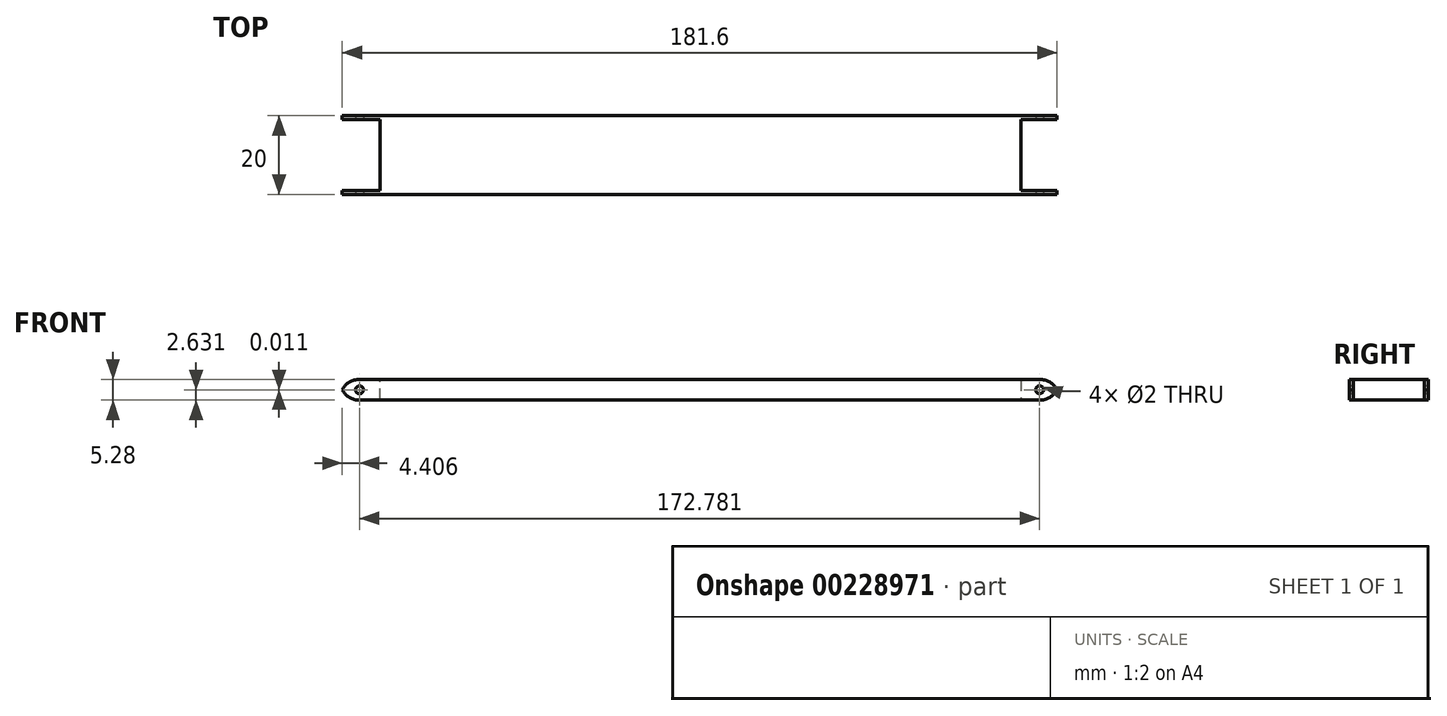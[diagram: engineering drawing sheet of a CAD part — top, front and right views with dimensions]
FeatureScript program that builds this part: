
annotation { "Feature Type Name" : "Feature", "Feature Type Description" : "" }
export const myFeature = defineFeature(function(context is Context, id is Id, definition is map)
    precondition{}
    {
        {
            var Q0;
            Q0=qCreatedBy(makeId("Front.planeOp"),FACE);
            var sketch = newSketch(context, id + "F0", { "sketchPlane" : qUnion([Q0])});
            skLineSegment(sketch, "E0.bottom", {"start": v(-74.93, 0) * mm, "end": v(107.85, 0) * mm});
            skLineSegment(sketch, "E0.top", {"start": v(-74.93, 5.28) * mm, "end": v(107.85, 5.28) * mm});
            skLineSegment(sketch, "E0.left", {"start": v(-74.93, 0) * mm, "end": v(-74.93, 5.28) * mm});
            skLineSegment(sketch, "E0.right", {"start": v(107.85, 0) * mm, "end": v(107.85, 5.28) * mm});
            skPoint(sketch, "E1", {"position": v(-74.93, 5.28) * mm});
            skPoint(sketch, "E2", {"position": v(-74.93, 0) * mm});
            skPoint(sketch, "E3", {"position": v(-69.93, 5.28) * mm});
            skPoint(sketch, "E4", {"position": v(-69.93, 0) * mm});
            skPoint(sketch, "E5", {"position": v(-74.36, 2.63) * mm});
            skPoint(sketch, "E6", {"position": v(-69.93, 2.63) * mm});
            skPoint(sketch, "E7", {"position": v(102.85, 5.28) * mm});
            skPoint(sketch, "E8", {"position": v(102.85, 0) * mm});
            skPoint(sketch, "E9", {"position": v(107.26, 2.64) * mm});
            skPoint(sketch, "E10", {"position": v(102.85, 2.64) * mm});
            skSolve(sketch);
        }
        {
            var Q0;
            Q0=makeQuery(id+"F0.imprint","IMPRINT",FACE,{"disambiguationData":[TD([[makeQuery(id+"F0.imprint","IMPRINT",EDGE,{"derivedFrom":sQuery(id+"F0.wireOp",EDGE,"E0.bottom")}),1.0]])]});
            extrude(context, id + "F1", {"entities" : qUnion([Q0]), "oppositeDirection" : true, "depth" : 20 * mm});
        }
        {
            var Q0;
            Q0=makeQuery(id+"F1.opExtrude","SWEPT_EDGE",EDGE,{"disambiguationData":[OSD([sQuery(id+"F0.wireOp",EDGE,"E0.top"),sQuery(id+"F0.wireOp",EDGE,"E0.left")])]});
            var Q1;
            Q1=makeQuery(id+"F1.opExtrude","SWEPT_EDGE",EDGE,{"disambiguationData":[OSD([sQuery(id+"F0.wireOp",EDGE,"E0.bottom"),sQuery(id+"F0.wireOp",EDGE,"E0.left")])]});
            fillet(context, id + "F2", {"entities" : qUnion([Q0, Q1]), "radius" : 5 * mm, "tangentPropagation" : true, "allowEdgeOverflow" : false});
        }
        {
            var Q0;
            Q0=sQuery(id+"F0.wireOp",VERTEX,"E6");
            var Q1;
            Q1=makeQuery(id+"F1.opExtrude","SWEPT_BODY",BODY,{"disambiguationData":[OSD([sQuery(id+"F0.wireOp",EDGE,"E0.bottom"),sQuery(id+"F0.wireOp",EDGE,"E0.top"),sQuery(id+"F0.wireOp",EDGE,"E0.left"),sQuery(id+"F0.wireOp",EDGE,"E0.right")])]});
            hole(context, id + "F3", {"style" : HoleStyle.SIMPLE, "endStyle" : HoleEndStyle.THROUGH, "holeDiameter" : 2 * mm, "locations" : qUnion([Q0]), "scope" : qUnion([Q1]), "isTappedThrough" : true});
        }
        {
            var Q0;
            Q0=makeQuery(id+"F1.opExtrude","SWEPT_EDGE",EDGE,{"disambiguationData":[OSD([sQuery(id+"F0.wireOp",EDGE,"E0.top"),sQuery(id+"F0.wireOp",EDGE,"E0.right")])]});
            var Q1;
            Q1=makeQuery(id+"F1.opExtrude","SWEPT_EDGE",EDGE,{"disambiguationData":[OSD([sQuery(id+"F0.wireOp",EDGE,"E0.bottom"),sQuery(id+"F0.wireOp",EDGE,"E0.right")])]});
            fillet(context, id + "F4", {"entities" : qUnion([Q0, Q1]), "radius" : 5 * mm, "tangentPropagation" : true, "allowEdgeOverflow" : false});
        }
        {
            var Q0;
            Q0=sQuery(id+"F0.wireOp",VERTEX,"E10");
            var Q1;
            Q1=makeQuery(id+"F1.opExtrude","SWEPT_BODY",BODY,{"disambiguationData":[OSD([sQuery(id+"F0.wireOp",EDGE,"E0.bottom"),sQuery(id+"F0.wireOp",EDGE,"E0.top"),sQuery(id+"F0.wireOp",EDGE,"E0.left"),sQuery(id+"F0.wireOp",EDGE,"E0.right")])]});
            hole(context, id + "F5", {"style" : HoleStyle.SIMPLE, "endStyle" : HoleEndStyle.THROUGH, "holeDiameter" : 2 * mm, "locations" : qUnion([Q0]), "scope" : qUnion([Q1]), "isTappedThrough" : true});
        }
        {
            var Q0;
            Q0=qCreatedBy(makeId("Front.planeOp"),FACE);
            var sketch = newSketch(context, id + "F6", { "sketchPlane" : qUnion([Q0])});
            skLineSegment(sketch, "E11.bottom", {"start": v(-76.4, 0) * mm, "end": v(-65.73, 0) * mm});
            skLineSegment(sketch, "E11.top", {"start": v(-76.4, 5.7) * mm, "end": v(-65.73, 5.7) * mm});
            skLineSegment(sketch, "E11.left", {"start": v(-76.4, 0) * mm, "end": v(-76.4, 5.7) * mm});
            skLineSegment(sketch, "E11.right", {"start": v(-65.73, 0) * mm, "end": v(-65.73, 5.7) * mm});
            skLineSegment(sketch, "E12.bottom", {"start": v(97.05, 6.55) * mm, "end": v(107.22, 6.55) * mm});
            skLineSegment(sketch, "E12.top", {"start": v(97.05, -1.53) * mm, "end": v(107.22, -1.53) * mm});
            skLineSegment(sketch, "E12.left", {"start": v(97.05, 6.55) * mm, "end": v(97.05, -1.53) * mm});
            skLineSegment(sketch, "E12.right", {"start": v(107.22, 6.55) * mm, "end": v(107.22, -1.53) * mm});
            skSolve(sketch);
        }
        {
            var Q0;
            Q0=makeQuery(id+"F1.opExtrude","SWEPT_BODY",BODY,{"disambiguationData":[OSD([sQuery(id+"F0.wireOp",EDGE,"E0.bottom"),sQuery(id+"F0.wireOp",EDGE,"E0.top"),sQuery(id+"F0.wireOp",EDGE,"E0.left"),sQuery(id+"F0.wireOp",EDGE,"E0.right")])]});
            transform(context, id + "F7", {"entities" : qUnion([Q0]), "transformType" : TransformType.TRANSLATION_3D, "dx" : -1 * mm, "dy" : 1 * mm, "dz" : 0 * mm, "makeCopy" : false});
        }
        {
            var Q0;
            Q0=makeQuery(id+"F1.opExtrude","SWEPT_BODY",BODY,{"disambiguationData":[OSD([sQuery(id+"F0.wireOp",EDGE,"E0.bottom"),sQuery(id+"F0.wireOp",EDGE,"E0.top"),sQuery(id+"F0.wireOp",EDGE,"E0.left"),sQuery(id+"F0.wireOp",EDGE,"E0.right")])]});
            transform(context, id + "F8", {"entities" : qUnion([Q0]), "transformType" : TransformType.TRANSLATION_3D, "dx" : 0 * mm, "dy" : -2 * mm, "dz" : 0 * mm, "makeCopy" : false});
        }
        {
            var Q0;
            Q0=makeQuery(id+"F6.imprint","IMPRINT",FACE,{"disambiguationData":[TD([[makeQuery(id+"F6.imprint","IMPRINT",EDGE,{"derivedFrom":sQuery(id+"F6.wireOp",EDGE,"E11.bottom")}),1.0]])]});
            extrude(context, id + "F9", {"entities" : qUnion([Q0]), "operationType" : NewBodyOperationType.REMOVE, "oppositeDirection" : true, "depth" : 18 * mm});
        }
        {
            var Q0;
            Q0=makeQuery(id+"F6.imprint","IMPRINT",FACE,{"disambiguationData":[TD([[makeQuery(id+"F6.imprint","IMPRINT",EDGE,{"derivedFrom":sQuery(id+"F6.wireOp",EDGE,"E12.bottom")}),-1.0]])]});
            extrude(context, id + "F10", {"entities" : qUnion([Q0]), "operationType" : NewBodyOperationType.REMOVE, "oppositeDirection" : true, "depth" : 18 * mm});
        }
    });
